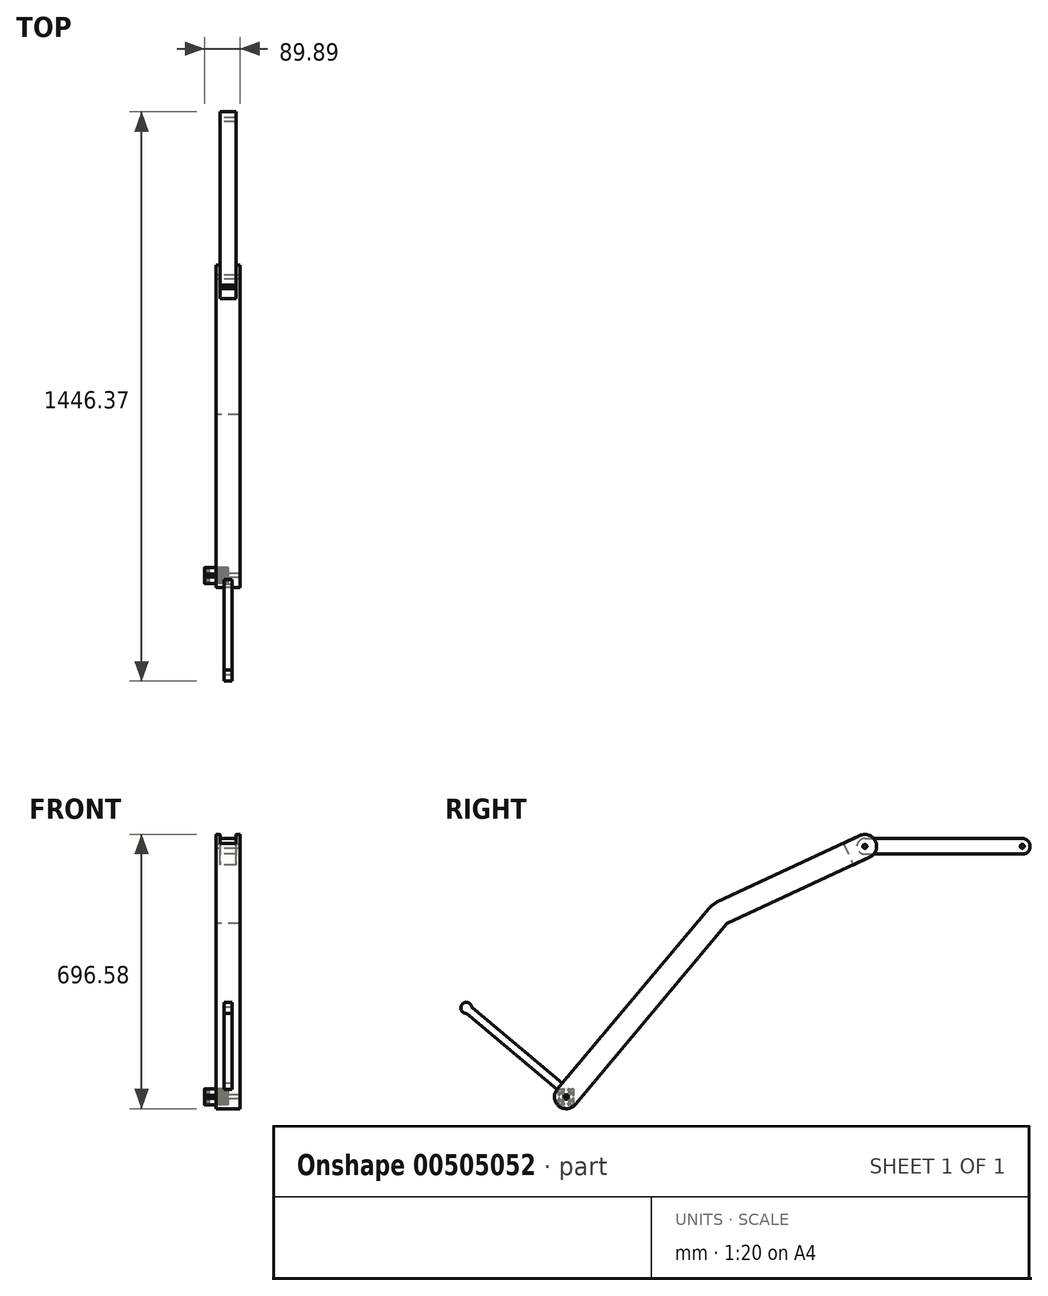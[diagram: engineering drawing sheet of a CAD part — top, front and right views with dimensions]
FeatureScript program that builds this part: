
annotation { "Feature Type Name" : "Feature", "Feature Type Description" : "" }
export const myFeature = defineFeature(function(context is Context, id is Id, definition is map)
    precondition{}
    {
        {
            var Q0;
            Q0=qCreatedBy(makeId("Right.planeOp"),FACE);
            var sketch = newSketch(context, id + "F0", { "sketchPlane" : qUnion([Q0])});
            skCircle(sketch, "E0", {"center": v(0, 0) * mm, "radius": 5 * mm});
            skArc(sketch, "E1", {"start": v(-22.98, 19.28) * mm, "mid": v(-19.28, -22.98) * mm, "end": v(22.98, -19.28) * mm});
            skLineSegment(sketch, "E2", {"start": v(-22.98, 19.28) * mm, "end": v(362.7, 478.91) * mm});
            skLineSegment(sketch, "E3", {"start": v(22.98, -19.28) * mm, "end": v(408.65, 440.34) * mm});
            skLineSegment(sketch, "E4", {"start": v(0, 0) * mm, "end": v(-104.18, 0) * mm, "construction": true});
            skLineSegment(sketch, "E5", {"start": v(408.65, 440.34) * mm, "end": v(771.18, 609.4) * mm});
            skLineSegment(sketch, "E6", {"start": v(745.82, 663.77) * mm, "end": v(383.3, 494.72) * mm});
            skArc(sketch, "E7", {"start": v(362.7, 478.91) * mm, "mid": v(372.13, 487.94) * mm, "end": v(383.3, 494.72) * mm});
            skLineSegment(sketch, "E8", {"start": v(383.3, 494.72) * mm, "end": v(408.65, 440.34) * mm, "construction": true});
            skArc(sketch, "E9", {"start": v(745.82, 663.77) * mm, "mid": v(785.69, 649.26) * mm, "end": v(771.18, 609.4) * mm});
            skCircle(sketch, "E10", {"center": v(758.5, 636.58) * mm, "radius": 5 * mm});
            skLineSegment(sketch, "E11", {"start": v(-22.98, 19.28) * mm, "end": v(-252.8, 212.12) * mm});
            skLineSegment(sketch, "E12", {"start": v(-252.8, 212.12) * mm, "end": v(-239.94, 227.44) * mm, "construction": true});
            skLineSegment(sketch, "E13", {"start": v(-239.94, 227.44) * mm, "end": v(-10.13, 34.6) * mm});
            skArc(sketch, "E14", {"start": v(-239.94, 227.44) * mm, "mid": v(-264.6, 235.08) * mm, "end": v(-252.8, 212.12) * mm});
            skSolve(sketch);
        }
        {
            var Q0;
            Q0=qCreatedBy(makeId("Right.planeOp"),FACE);
            var sketch = newSketch(context, id + "F1", { "sketchPlane" : qUnion([Q0])});
            skPoint(sketch, "E15.0", {"position": v(758.5, 636.58) * mm});
            skCircle(sketch, "E16.0", {"center": v(758.5, 636.58) * mm, "radius": 5 * mm});
            skLineSegment(sketch, "E17", {"start": v(758.5, 636.58) * mm, "end": v(758.5, 656.58) * mm});
            skArc(sketch, "E18", {"start": v(758.5, 656.58) * mm, "mid": v(738.5, 636.58) * mm, "end": v(758.5, 616.58) * mm});
            skLineSegment(sketch, "E19", {"start": v(758.5, 656.58) * mm, "end": v(1158.5, 656.58) * mm});
            skLineSegment(sketch, "E20", {"start": v(758.5, 616.58) * mm, "end": v(1158.5, 616.58) * mm});
            skLineSegment(sketch, "E21", {"start": v(1158.5, 656.58) * mm, "end": v(1158.5, 616.58) * mm, "construction": true});
            skArc(sketch, "E22", {"start": v(1158.5, 656.58) * mm, "mid": v(1178.5, 636.58) * mm, "end": v(1158.5, 616.58) * mm});
            skCircle(sketch, "E23", {"center": v(1158.5, 636.58) * mm, "radius": 5 * mm});
            skSolve(sketch);
        }
        {
            var Q0;
            Q0=makeQuery(id+"F0.imprint","IMPRINT",FACE,{"disambiguationData":[TD([[makeQuery(id+"F0.imprint","IMPRINT",EDGE,{"derivedFrom":sQuery(id+"F0.wireOp",EDGE,"E0")}),-1.0]])]});
            extrude(context, id + "F2", {"entities" : qUnion([Q0]), "endBound" : BoundingType.SYMMETRIC, "depth" : 60 * mm});
        }
        {
            var Q0;
            Q0=makeQuery(id+"F2.opExtrude","CAP_VERTEX",VERTEX,{"disambiguationData":[OSD([sQuery(id+"F0.wireOp",EDGE,"E6"),sQuery(id+"F0.wireOp",EDGE,"E9")])],"isStart":false});
            var Q1;
            Q1=makeQuery(id+"F2.opExtrude","CAP_VERTEX",VERTEX,{"disambiguationData":[OSD([sQuery(id+"F0.wireOp",EDGE,"E5"),sQuery(id+"F0.wireOp",EDGE,"E9")])],"isStart":false});
            var Q2;
            Q2=makeQuery(id+"F2.opExtrude","CAP_VERTEX",VERTEX,{"disambiguationData":[OSD([sQuery(id+"F0.wireOp",EDGE,"E5"),sQuery(id+"F0.wireOp",EDGE,"E9")])],"isStart":true});
            cPlane(context, id + "F3", {"entities" : qUnion([Q0, Q1, Q2]), "cplaneType" : CPlaneType.THREE_POINT, "offset" : 25 * mm, "width" : 150 * mm, "height" : 150 * mm});
        }
        {
            var Q0;
            Q0=qCreatedBy(id+"F3.planeOp",FACE);
            var sketch = newSketch(context, id + "F4", { "sketchPlane" : qUnion([Q0])});
            skPoint(sketch, "E24.0", {"position": v(0, 256.38) * mm});
            skLineSegment(sketch, "E25", {"start": v(0, 256.38) * mm, "end": v(20, 256.38) * mm, "construction": true});
            skLineSegment(sketch, "E26.0", {"start": v(30, 286.38) * mm, "end": v(-30, 286.38) * mm, "construction": true});
            skLineSegment(sketch, "E27.0", {"start": v(30, 226.38) * mm, "end": v(-30, 226.38) * mm, "construction": true});
            skLineSegment(sketch, "E28.bottom", {"start": v(20, 286.38) * mm, "end": v(-20, 286.38) * mm});
            skLineSegment(sketch, "E28.top", {"start": v(20, 226.38) * mm, "end": v(-20, 226.38) * mm});
            skLineSegment(sketch, "E28.left", {"start": v(20, 286.38) * mm, "end": v(20, 226.38) * mm});
            skLineSegment(sketch, "E28.right", {"start": v(-20, 286.38) * mm, "end": v(-20, 226.38) * mm});
            skSolve(sketch);
        }
        {
            var Q0;
            Q0 = qSketchRegion(id + "F4", true);
            extrude(context, id + "F5", {"entities" : qUnion([Q0]), "operationType" : NewBodyOperationType.REMOVE, "depth" : 46.5 * mm, "hasSecondDirection" : true, "secondDirectionOppositeDirection" : true, "secondDirectionDepth" : 41.1 * mm});
        }
        {
            var Q0;
            Q0 = qSketchRegion(id + "F1", true);
            extrude(context, id + "F6", {"entities" : qUnion([Q0]), "endBound" : BoundingType.SYMMETRIC, "depth" : 40 * mm});
        }
        {
            var Q0;
            Q0=qCreatedBy(makeId("Right.planeOp"),FACE);
            var sketch = newSketch(context, id + "F7", { "sketchPlane" : qUnion([Q0])});
            skCircle(sketch, "E29.0", {"center": v(0, 0) * mm, "radius": 5 * mm});
            skSolve(sketch);
        }
        {
            var Q0;
            Q0 = qSketchRegion(id + "F7", true);
            extrude(context, id + "F8", {"entities" : qUnion([Q0]), "endBound" : BoundingType.SYMMETRIC, "depth" : 60 * mm});
        }
        {
            var Q0;
            Q0=makeQuery(id+"F8.opExtrude","CAP_EDGE",EDGE,{"disambiguationData":[OSD([sQuery(id+"F7.wireOp",EDGE,"E29.0")])],"isStart":true});
            var Q1;
            Q1=makeQuery(id+"F8.opExtrude","CAP_EDGE",EDGE,{"disambiguationData":[OSD([sQuery(id+"F7.wireOp",EDGE,"E29.0")])],"isStart":false});
            chamfer(context, id + "F9", {"entities" : qUnion([Q0, Q1]), "width" : 1 * mm, "tangentPropagation" : true});
        }
        {
            var Q0;
            {var subQ0=sQuery(id+"F0.wireOp",EDGE,"E11");Q0=makeQuery(id+"F0.imprint","IMPRINT",FACE,{"disambiguationData":[TD([[makeQuery(id+"F0.imprint","IMPRINT",EDGE,{"derivedFrom":subQ0}),-1.0]])]});}
            extrude(context, id + "F10", {"entities" : qUnion([Q0]), "operationType" : NewBodyOperationType.ADD, "endBound" : BoundingType.SYMMETRIC, "depth" : 20 * mm});
        }
        {
            var Q0;
            Q0=qCreatedBy(makeId("Right.planeOp"),FACE);
            var sketch = newSketch(context, id + "F11", { "sketchPlane" : qUnion([Q0])});
            skLineSegment(sketch, "E30", {"start": v(-10.29, 12.4) * mm, "end": v(-10.55, 12.74) * mm});
            skLineSegment(sketch, "E31", {"start": v(10.55, -12.74) * mm, "end": v(10.29, -12.4) * mm});
            skLineSegment(sketch, "E32", {"start": v(10.76, 9.6) * mm, "end": v(9.6, 10.76) * mm});
            skLineSegment(sketch, "E33", {"start": v(-10.33, -11.73) * mm, "end": v(-11.73, -10.33) * mm});
            skLineSegment(sketch, "E34", {"start": v(-9.6, -10.76) * mm, "end": v(-10.76, -9.6) * mm});
            skLineSegment(sketch, "E35", {"start": v(11.73, 10.33) * mm, "end": v(10.33, 11.73) * mm});
            skLineSegment(sketch, "E36", {"start": v(12.74, -10.55) * mm, "end": v(12.4, -10.29) * mm});
            skLineSegment(sketch, "E37", {"start": v(-12.4, 10.29) * mm, "end": v(-12.74, 10.55) * mm});
            skLineSegment(sketch, "E38", {"start": v(-16, -20) * mm, "end": v(-5.5, -20) * mm});
            skLineSegment(sketch, "E39", {"start": v(5.5, -20) * mm, "end": v(16, -20) * mm});
            skLineSegment(sketch, "E40", {"start": v(-16, -18.8) * mm, "end": v(-11.7, -18.8) * mm});
            skLineSegment(sketch, "E41", {"start": v(11.7, -18.8) * mm, "end": v(16, -18.8) * mm});
            skLineSegment(sketch, "E42", {"start": v(-7.5, -18) * mm, "end": v(-7.25, -18) * mm});
            skLineSegment(sketch, "E43", {"start": v(7.25, -18) * mm, "end": v(7.5, -18) * mm});
            skLineSegment(sketch, "E44", {"start": v(-6.75, -15.5) * mm, "end": v(-5, -15.5) * mm});
            skLineSegment(sketch, "E45", {"start": v(5, -15.5) * mm, "end": v(6.75, -15.5) * mm});
            skLineSegment(sketch, "E46", {"start": v(-18.3, -11.2) * mm, "end": v(-14.67, -11.2) * mm});
            skLineSegment(sketch, "E47", {"start": v(14.67, -11.2) * mm, "end": v(18.3, -11.2) * mm});
            skLineSegment(sketch, "E48", {"start": v(-15.5, -10) * mm, "end": v(-14.72, -10) * mm});
            skLineSegment(sketch, "E49", {"start": v(14.72, -10) * mm, "end": v(15.5, -10) * mm});
            skLineSegment(sketch, "E50", {"start": v(-2.2, -7.75) * mm, "end": v(2.2, -7.75) * mm});
            skLineSegment(sketch, "E51", {"start": v(-17.75, -7) * mm, "end": v(-15.75, -7) * mm});
            skLineSegment(sketch, "E52", {"start": v(15.75, -7) * mm, "end": v(17.75, -7) * mm});
            skLineSegment(sketch, "E53", {"start": v(-18.5, -4) * mm, "end": v(-16.5, -4) * mm});
            skLineSegment(sketch, "E54", {"start": v(16.5, -4) * mm, "end": v(18.5, -4) * mm});
            skLineSegment(sketch, "E55", {"start": v(-6.1, -2.5) * mm, "end": v(-4.6, -2.5) * mm});
            skLineSegment(sketch, "E56", {"start": v(4.6, -2.5) * mm, "end": v(6.1, -2.5) * mm});
            skLineSegment(sketch, "E57", {"start": v(4.6, 2.5) * mm, "end": v(6.1, 2.5) * mm});
            skLineSegment(sketch, "E58", {"start": v(-6.1, 2.5) * mm, "end": v(-4.6, 2.5) * mm});
            skLineSegment(sketch, "E59", {"start": v(-18.5, 4) * mm, "end": v(-16.5, 4) * mm});
            skLineSegment(sketch, "E60", {"start": v(16.5, 4) * mm, "end": v(18.5, 4) * mm});
            skLineSegment(sketch, "E61", {"start": v(-17.75, 7) * mm, "end": v(-15.75, 7) * mm});
            skLineSegment(sketch, "E62", {"start": v(15.75, 7) * mm, "end": v(17.75, 7) * mm});
            skLineSegment(sketch, "E63", {"start": v(-2.2, 7.75) * mm, "end": v(2.2, 7.75) * mm});
            skLineSegment(sketch, "E64", {"start": v(-15.5, 10) * mm, "end": v(-14.72, 10) * mm});
            skLineSegment(sketch, "E65", {"start": v(14.72, 10) * mm, "end": v(15.5, 10) * mm});
            skLineSegment(sketch, "E66", {"start": v(-18.3, 11.2) * mm, "end": v(-14.67, 11.2) * mm});
            skLineSegment(sketch, "E67", {"start": v(14.67, 11.2) * mm, "end": v(18.3, 11.2) * mm});
            skLineSegment(sketch, "E68", {"start": v(-6.75, 15.5) * mm, "end": v(-5, 15.5) * mm});
            skLineSegment(sketch, "E69", {"start": v(5, 15.5) * mm, "end": v(6.75, 15.5) * mm});
            skLineSegment(sketch, "E70", {"start": v(-7.5, 18) * mm, "end": v(-7.25, 18) * mm});
            skLineSegment(sketch, "E71", {"start": v(7.25, 18) * mm, "end": v(7.5, 18) * mm});
            skLineSegment(sketch, "E72", {"start": v(-16, 18.8) * mm, "end": v(-11.7, 18.8) * mm});
            skLineSegment(sketch, "E73", {"start": v(11.7, 18.8) * mm, "end": v(16, 18.8) * mm});
            skLineSegment(sketch, "E74", {"start": v(5.5, 20) * mm, "end": v(16, 20) * mm});
            skLineSegment(sketch, "E75", {"start": v(-16, 20) * mm, "end": v(-5.5, 20) * mm});
            skLineSegment(sketch, "E76", {"start": v(12.4, 10.29) * mm, "end": v(12.74, 10.55) * mm});
            skLineSegment(sketch, "E77", {"start": v(-12.74, -10.55) * mm, "end": v(-12.4, -10.29) * mm});
            skLineSegment(sketch, "E78", {"start": v(9.6, -10.76) * mm, "end": v(10.76, -9.6) * mm});
            skLineSegment(sketch, "E79", {"start": v(-10.76, 9.6) * mm, "end": v(-9.6, 10.76) * mm});
            skLineSegment(sketch, "E80", {"start": v(10.33, -11.73) * mm, "end": v(11.73, -10.33) * mm});
            skLineSegment(sketch, "E81", {"start": v(-11.73, 10.33) * mm, "end": v(-10.33, 11.73) * mm});
            skLineSegment(sketch, "E82", {"start": v(10.29, 12.4) * mm, "end": v(10.55, 12.74) * mm});
            skLineSegment(sketch, "E83", {"start": v(-10.55, -12.74) * mm, "end": v(-10.29, -12.4) * mm});
            skLineSegment(sketch, "E84", {"start": v(-20, 5.5) * mm, "end": v(-20, 16) * mm});
            skLineSegment(sketch, "E85", {"start": v(-20, -16) * mm, "end": v(-20, -5.5) * mm});
            skLineSegment(sketch, "E86", {"start": v(-18.8, 11.7) * mm, "end": v(-18.8, 16) * mm});
            skLineSegment(sketch, "E87", {"start": v(-18.8, -16) * mm, "end": v(-18.8, -11.7) * mm});
            skLineSegment(sketch, "E88", {"start": v(-18, 7.25) * mm, "end": v(-18, 7.5) * mm});
            skLineSegment(sketch, "E89", {"start": v(-18, -7.5) * mm, "end": v(-18, -7.25) * mm});
            skLineSegment(sketch, "E90", {"start": v(-15.5, 5) * mm, "end": v(-15.5, 6.75) * mm});
            skLineSegment(sketch, "E91", {"start": v(-15.5, -6.75) * mm, "end": v(-15.5, -5) * mm});
            skLineSegment(sketch, "E92", {"start": v(-11.2, 14.67) * mm, "end": v(-11.2, 18.3) * mm});
            skLineSegment(sketch, "E93", {"start": v(-11.2, -18.3) * mm, "end": v(-11.2, -14.67) * mm});
            skLineSegment(sketch, "E94", {"start": v(-10, 14.72) * mm, "end": v(-10, 15.5) * mm});
            skLineSegment(sketch, "E95", {"start": v(-10, -15.5) * mm, "end": v(-10, -14.72) * mm});
            skLineSegment(sketch, "E96", {"start": v(-7.75, -2.2) * mm, "end": v(-7.75, 2.2) * mm});
            skLineSegment(sketch, "E97", {"start": v(-7, 15.75) * mm, "end": v(-7, 17.75) * mm});
            skLineSegment(sketch, "E98", {"start": v(-7, -17.75) * mm, "end": v(-7, -15.75) * mm});
            skLineSegment(sketch, "E99", {"start": v(-4, 16.5) * mm, "end": v(-4, 18.5) * mm});
            skLineSegment(sketch, "E100", {"start": v(-4, -18.5) * mm, "end": v(-4, -16.5) * mm});
            skLineSegment(sketch, "E101", {"start": v(-2.5, 4.6) * mm, "end": v(-2.5, 6.1) * mm});
            skLineSegment(sketch, "E102", {"start": v(-2.5, -6.1) * mm, "end": v(-2.5, -4.6) * mm});
            skLineSegment(sketch, "E103", {"start": v(2.5, 4.6) * mm, "end": v(2.5, 6.1) * mm});
            skLineSegment(sketch, "E104", {"start": v(2.5, -6.1) * mm, "end": v(2.5, -4.6) * mm});
            skLineSegment(sketch, "E105", {"start": v(4, 16.5) * mm, "end": v(4, 18.5) * mm});
            skLineSegment(sketch, "E106", {"start": v(4, -18.5) * mm, "end": v(4, -16.5) * mm});
            skLineSegment(sketch, "E107", {"start": v(7, 15.75) * mm, "end": v(7, 17.75) * mm});
            skLineSegment(sketch, "E108", {"start": v(7, -17.75) * mm, "end": v(7, -15.75) * mm});
            skLineSegment(sketch, "E109", {"start": v(7.75, -2.2) * mm, "end": v(7.75, 2.2) * mm});
            skLineSegment(sketch, "E110", {"start": v(10, 14.72) * mm, "end": v(10, 15.5) * mm});
            skLineSegment(sketch, "E111", {"start": v(10, -15.5) * mm, "end": v(10, -14.72) * mm});
            skLineSegment(sketch, "E112", {"start": v(11.2, 14.67) * mm, "end": v(11.2, 18.3) * mm});
            skLineSegment(sketch, "E113", {"start": v(11.2, -18.3) * mm, "end": v(11.2, -14.67) * mm});
            skLineSegment(sketch, "E114", {"start": v(15.5, -6.75) * mm, "end": v(15.5, -5) * mm});
            skLineSegment(sketch, "E115", {"start": v(15.5, 5) * mm, "end": v(15.5, 6.75) * mm});
            skLineSegment(sketch, "E116", {"start": v(18, -7.5) * mm, "end": v(18, -7.25) * mm});
            skLineSegment(sketch, "E117", {"start": v(18, 7.25) * mm, "end": v(18, 7.5) * mm});
            skLineSegment(sketch, "E118", {"start": v(18.8, 11.7) * mm, "end": v(18.8, 16) * mm});
            skLineSegment(sketch, "E119", {"start": v(18.8, -16) * mm, "end": v(18.8, -11.7) * mm});
            skLineSegment(sketch, "E120", {"start": v(20, -16) * mm, "end": v(20, -5.5) * mm});
            skLineSegment(sketch, "E121", {"start": v(20, 5.5) * mm, "end": v(20, 16) * mm});
            skArc(sketch, "E122", {"start": v(-8.54, 4.58) * mm, "mid": v(-10.85, 7.26) * mm, "end": v(-13.51, 9.6) * mm});
            skArc(sketch, "E123", {"start": v(-13.51, -9.6) * mm, "mid": v(-10.85, -7.26) * mm, "end": v(-8.54, -4.58) * mm});
            skArc(sketch, "E124", {"start": v(-7.6, 5.38) * mm, "mid": v(-9.09, 7.2) * mm, "end": v(-10.75, 8.88) * mm});
            skArc(sketch, "E125", {"start": v(-10.75, -8.88) * mm, "mid": v(-9.09, -7.2) * mm, "end": v(-7.6, -5.38) * mm});
            skArc(sketch, "E126", {"start": v(-18.5, -4) * mm, "mid": v(-19.56, -4.44) * mm, "end": v(-20, -5.5) * mm});
            skArc(sketch, "E127", {"start": v(-20, 5.5) * mm, "mid": v(-19.56, 4.44) * mm, "end": v(-18.5, 4) * mm});
            skArc(sketch, "E128", {"start": v(-18.8, 11.7) * mm, "mid": v(-18.65, 11.35) * mm, "end": v(-18.3, 11.2) * mm});
            skArc(sketch, "E129", {"start": v(-18.3, -11.2) * mm, "mid": v(-18.65, -11.35) * mm, "end": v(-18.8, -11.7) * mm});
            skArc(sketch, "E130", {"start": v(-17.75, -7) * mm, "mid": v(-17.93, -7.07) * mm, "end": v(-18, -7.25) * mm});
            skArc(sketch, "E131", {"start": v(-18, 7.25) * mm, "mid": v(-17.93, 7.07) * mm, "end": v(-17.75, 7) * mm});
            skArc(sketch, "E132", {"start": v(-15.5, -5) * mm, "mid": v(-15.8, -4.3) * mm, "end": v(-16.5, -4) * mm});
            skArc(sketch, "E133", {"start": v(-16.5, 4) * mm, "mid": v(-15.8, 4.3) * mm, "end": v(-15.5, 5) * mm});
            skArc(sketch, "E134", {"start": v(-20, -16) * mm, "mid": v(-18.83, -18.83) * mm, "end": v(-16, -20) * mm});
            skArc(sketch, "E135", {"start": v(-16, 18.8) * mm, "mid": v(-17.98, 17.98) * mm, "end": v(-18.8, 16) * mm});
            skArc(sketch, "E136", {"start": v(-16, 20) * mm, "mid": v(-18.83, 18.83) * mm, "end": v(-20, 16) * mm});
            skArc(sketch, "E137", {"start": v(-18.8, -16) * mm, "mid": v(-17.98, -17.98) * mm, "end": v(-16, -18.8) * mm});
            skArc(sketch, "E138", {"start": v(-15.75, -7) * mm, "mid": v(-15.57, -6.93) * mm, "end": v(-15.5, -6.75) * mm});
            skArc(sketch, "E139", {"start": v(-15.5, 6.75) * mm, "mid": v(-15.57, 6.93) * mm, "end": v(-15.75, 7) * mm});
            skArc(sketch, "E140", {"start": v(-18, -7.5) * mm, "mid": v(-17.27, -9.27) * mm, "end": v(-15.5, -10) * mm});
            skArc(sketch, "E141", {"start": v(-15.5, 10) * mm, "mid": v(-17.27, 9.27) * mm, "end": v(-18, 7.5) * mm});
            skArc(sketch, "E142", {"start": v(-14.72, -10) * mm, "mid": v(-14.08, -9.9) * mm, "end": v(-13.51, -9.6) * mm});
            skArc(sketch, "E143", {"start": v(-13.51, 9.6) * mm, "mid": v(-14.08, 9.9) * mm, "end": v(-14.72, 10) * mm});
            skArc(sketch, "E144", {"start": v(-12.74, 10.55) * mm, "mid": v(-13.65, 11.03) * mm, "end": v(-14.67, 11.2) * mm});
            skArc(sketch, "E145", {"start": v(-14.67, -11.2) * mm, "mid": v(-13.65, -11.03) * mm, "end": v(-12.74, -10.55) * mm});
            skArc(sketch, "E146", {"start": v(-12.4, 10.29) * mm, "mid": v(-12.06, 10.18) * mm, "end": v(-11.73, 10.33) * mm});
            skArc(sketch, "E147", {"start": v(-11.73, -10.33) * mm, "mid": v(-12.06, -10.18) * mm, "end": v(-12.4, -10.29) * mm});
            skArc(sketch, "E148", {"start": v(-7.59, -5.38) * mm, "mid": v(-6.93, -4.22) * mm, "end": v(-6.6, -2.94) * mm});
            skArc(sketch, "E149", {"start": v(-8.54, -4.58) * mm, "mid": v(-7.95, -3.45) * mm, "end": v(-7.75, -2.2) * mm});
            skArc(sketch, "E150", {"start": v(-7.75, 2.2) * mm, "mid": v(-7.95, 3.45) * mm, "end": v(-8.54, 4.58) * mm});
            skArc(sketch, "E151", {"start": v(-6.6, 2.94) * mm, "mid": v(-6.93, 4.22) * mm, "end": v(-7.6, 5.38) * mm});
            skArc(sketch, "E152", {"start": v(-11.2, 18.3) * mm, "mid": v(-11.35, 18.65) * mm, "end": v(-11.7, 18.8) * mm});
            skArc(sketch, "E153", {"start": v(-11.7, -18.8) * mm, "mid": v(-11.35, -18.65) * mm, "end": v(-11.2, -18.3) * mm});
            skArc(sketch, "E154", {"start": v(-10.33, 11.73) * mm, "mid": v(-10.18, 12.06) * mm, "end": v(-10.29, 12.4) * mm});
            skArc(sketch, "E155", {"start": v(-10.29, -12.4) * mm, "mid": v(-10.18, -12.06) * mm, "end": v(-10.33, -11.73) * mm});
            skArc(sketch, "E156", {"start": v(-10.75, -8.88) * mm, "mid": v(-10.9, -9.24) * mm, "end": v(-10.76, -9.6) * mm});
            skArc(sketch, "E157", {"start": v(-10.76, 9.6) * mm, "mid": v(-10.9, 9.24) * mm, "end": v(-10.75, 8.88) * mm});
            skArc(sketch, "E158", {"start": v(9.6, -13.51) * mm, "mid": v(7.26, -10.85) * mm, "end": v(4.58, -8.54) * mm});
            skArc(sketch, "E159", {"start": v(8.88, -10.75) * mm, "mid": v(7.2, -9.09) * mm, "end": v(5.38, -7.6) * mm});
            skArc(sketch, "E160", {"start": v(5.38, 7.59) * mm, "mid": v(7.2, 9.09) * mm, "end": v(8.88, 10.75) * mm});
            skArc(sketch, "E161", {"start": v(4.58, 8.54) * mm, "mid": v(7.26, 10.85) * mm, "end": v(9.6, 13.51) * mm});
            skArc(sketch, "E162", {"start": v(-9.6, -10.76) * mm, "mid": v(-9.24, -10.9) * mm, "end": v(-8.88, -10.75) * mm});
            skArc(sketch, "E163", {"start": v(-8.88, 10.75) * mm, "mid": v(-9.24, 10.9) * mm, "end": v(-9.6, 10.76) * mm});
            skArc(sketch, "E164", {"start": v(-9.6, -13.51) * mm, "mid": v(-9.9, -14.08) * mm, "end": v(-10, -14.72) * mm});
            skArc(sketch, "E165", {"start": v(-11.2, 14.67) * mm, "mid": v(-11.03, 13.65) * mm, "end": v(-10.55, 12.74) * mm});
            skArc(sketch, "E166", {"start": v(-10, 14.72) * mm, "mid": v(-9.9, 14.08) * mm, "end": v(-9.6, 13.51) * mm});
            skArc(sketch, "E167", {"start": v(-10.55, -12.74) * mm, "mid": v(-11.03, -13.65) * mm, "end": v(-11.2, -14.67) * mm});
            skArc(sketch, "E168", {"start": v(-10, -15.5) * mm, "mid": v(-9.27, -17.27) * mm, "end": v(-7.5, -18) * mm});
            skArc(sketch, "E169", {"start": v(-7.5, 18) * mm, "mid": v(-9.27, 17.27) * mm, "end": v(-10, 15.5) * mm});
            skArc(sketch, "E170", {"start": v(-7.25, -18) * mm, "mid": v(-7.07, -17.93) * mm, "end": v(-7, -17.75) * mm});
            skArc(sketch, "E171", {"start": v(-7, 17.75) * mm, "mid": v(-7.07, 17.93) * mm, "end": v(-7.25, 18) * mm});
            skArc(sketch, "E172", {"start": v(-6.75, -15.5) * mm, "mid": v(-6.93, -15.57) * mm, "end": v(-7, -15.75) * mm});
            skArc(sketch, "E173", {"start": v(-7, 15.75) * mm, "mid": v(-6.93, 15.57) * mm, "end": v(-6.75, 15.5) * mm});
            skArc(sketch, "E174", {"start": v(-6.1, -2.5) * mm, "mid": v(-6.43, -2.62) * mm, "end": v(-6.6, -2.94) * mm});
            skArc(sketch, "E175", {"start": v(-6.6, 2.94) * mm, "mid": v(-6.43, 2.62) * mm, "end": v(-6.1, 2.5) * mm});
            skArc(sketch, "E176", {"start": v(-5.5, -20) * mm, "mid": v(-4.44, -19.56) * mm, "end": v(-4, -18.5) * mm});
            skArc(sketch, "E177", {"start": v(-4, 18.5) * mm, "mid": v(-4.44, 19.56) * mm, "end": v(-5.5, 20) * mm});
            skArc(sketch, "E178", {"start": v(-4, -16.5) * mm, "mid": v(-4.3, -15.8) * mm, "end": v(-5, -15.5) * mm});
            skArc(sketch, "E179", {"start": v(-5, 15.5) * mm, "mid": v(-4.3, 15.8) * mm, "end": v(-4, 16.5) * mm});
            skArc(sketch, "E180", {"start": v(-4.2, -2.73) * mm, "mid": v(-4.37, -2.56) * mm, "end": v(-4.6, -2.5) * mm});
            skArc(sketch, "E181", {"start": v(-4.6, 2.5) * mm, "mid": v(-4.37, 2.56) * mm, "end": v(-4.2, 2.73) * mm});
            skArc(sketch, "E182", {"start": v(-2.94, -6.6) * mm, "mid": v(-2.62, -6.43) * mm, "end": v(-2.5, -6.1) * mm});
            skArc(sketch, "E183", {"start": v(-2.5, -4.6) * mm, "mid": v(-2.56, -4.37) * mm, "end": v(-2.73, -4.2) * mm});
            skArc(sketch, "E184", {"start": v(-2.73, 4.2) * mm, "mid": v(-2.56, 4.37) * mm, "end": v(-2.5, 4.6) * mm});
            skArc(sketch, "E185", {"start": v(-2.5, 6.1) * mm, "mid": v(-2.62, 6.43) * mm, "end": v(-2.94, 6.6) * mm});
            skArc(sketch, "E186", {"start": v(-2.94, -6.6) * mm, "mid": v(-4.22, -6.93) * mm, "end": v(-5.38, -7.6) * mm});
            skArc(sketch, "E187", {"start": v(-5.38, 7.59) * mm, "mid": v(-4.22, 6.93) * mm, "end": v(-2.94, 6.6) * mm});
            skArc(sketch, "E188", {"start": v(-2.2, -7.75) * mm, "mid": v(-3.45, -7.95) * mm, "end": v(-4.58, -8.54) * mm});
            skArc(sketch, "E189", {"start": v(-4.58, 8.54) * mm, "mid": v(-3.45, 7.95) * mm, "end": v(-2.2, 7.75) * mm});
            skCircle(sketch, "E190", {"center": v(0, 0) * mm, "radius": 3.4 * mm});
            skArc(sketch, "E191", {"start": v(4.2, 2.73) * mm, "mid": v(3.54, 3.54) * mm, "end": v(2.73, 4.2) * mm});
            skArc(sketch, "E192", {"start": v(-2.73, 4.2) * mm, "mid": v(-3.54, 3.54) * mm, "end": v(-4.2, 2.73) * mm});
            skArc(sketch, "E193", {"start": v(-4.2, -2.73) * mm, "mid": v(-3.54, -3.54) * mm, "end": v(-2.73, -4.2) * mm});
            skArc(sketch, "E194", {"start": v(2.73, -4.2) * mm, "mid": v(3.54, -3.54) * mm, "end": v(4.2, -2.73) * mm});
            skArc(sketch, "E195", {"start": v(4.58, -8.54) * mm, "mid": v(3.45, -7.95) * mm, "end": v(2.2, -7.75) * mm});
            skArc(sketch, "E196", {"start": v(2.2, 7.75) * mm, "mid": v(3.45, 7.95) * mm, "end": v(4.58, 8.54) * mm});
            skArc(sketch, "E197", {"start": v(5.38, -7.59) * mm, "mid": v(4.22, -6.93) * mm, "end": v(2.94, -6.6) * mm});
            skArc(sketch, "E198", {"start": v(2.94, 6.6) * mm, "mid": v(4.22, 6.93) * mm, "end": v(5.38, 7.6) * mm});
            skArc(sketch, "E199", {"start": v(2.5, -6.1) * mm, "mid": v(2.62, -6.43) * mm, "end": v(2.94, -6.6) * mm});
            skArc(sketch, "E200", {"start": v(2.73, -4.2) * mm, "mid": v(2.56, -4.37) * mm, "end": v(2.5, -4.6) * mm});
            skArc(sketch, "E201", {"start": v(2.5, 4.6) * mm, "mid": v(2.56, 4.37) * mm, "end": v(2.73, 4.2) * mm});
            skArc(sketch, "E202", {"start": v(2.94, 6.6) * mm, "mid": v(2.62, 6.43) * mm, "end": v(2.5, 6.1) * mm});
            skArc(sketch, "E203", {"start": v(4.6, -2.5) * mm, "mid": v(4.37, -2.56) * mm, "end": v(4.2, -2.73) * mm});
            skArc(sketch, "E204", {"start": v(4.2, 2.73) * mm, "mid": v(4.37, 2.56) * mm, "end": v(4.6, 2.5) * mm});
            skArc(sketch, "E205", {"start": v(5, -15.5) * mm, "mid": v(4.3, -15.8) * mm, "end": v(4, -16.5) * mm});
            skArc(sketch, "E206", {"start": v(4, 16.5) * mm, "mid": v(4.3, 15.8) * mm, "end": v(5, 15.5) * mm});
            skArc(sketch, "E207", {"start": v(4, -18.5) * mm, "mid": v(4.44, -19.56) * mm, "end": v(5.5, -20) * mm});
            skArc(sketch, "E208", {"start": v(5.5, 20) * mm, "mid": v(4.44, 19.56) * mm, "end": v(4, 18.5) * mm});
            skArc(sketch, "E209", {"start": v(6.6, -2.94) * mm, "mid": v(6.43, -2.62) * mm, "end": v(6.1, -2.5) * mm});
            skArc(sketch, "E210", {"start": v(6.1, 2.5) * mm, "mid": v(6.43, 2.62) * mm, "end": v(6.6, 2.94) * mm});
            skArc(sketch, "E211", {"start": v(7, -15.75) * mm, "mid": v(6.93, -15.57) * mm, "end": v(6.75, -15.5) * mm});
            skArc(sketch, "E212", {"start": v(6.75, 15.5) * mm, "mid": v(6.93, 15.57) * mm, "end": v(7, 15.75) * mm});
            skArc(sketch, "E213", {"start": v(7, -17.75) * mm, "mid": v(7.07, -17.93) * mm, "end": v(7.25, -18) * mm});
            skArc(sketch, "E214", {"start": v(7.25, 18) * mm, "mid": v(7.07, 17.93) * mm, "end": v(7, 17.75) * mm});
            skArc(sketch, "E215", {"start": v(7.5, -18) * mm, "mid": v(9.27, -17.27) * mm, "end": v(10, -15.5) * mm});
            skArc(sketch, "E216", {"start": v(10, 15.5) * mm, "mid": v(9.27, 17.27) * mm, "end": v(7.5, 18) * mm});
            skArc(sketch, "E217", {"start": v(10.55, 12.74) * mm, "mid": v(11.03, 13.65) * mm, "end": v(11.2, 14.67) * mm});
            skArc(sketch, "E218", {"start": v(10, -14.72) * mm, "mid": v(9.9, -14.08) * mm, "end": v(9.6, -13.51) * mm});
            skArc(sketch, "E219", {"start": v(11.2, -14.67) * mm, "mid": v(11.03, -13.65) * mm, "end": v(10.55, -12.74) * mm});
            skArc(sketch, "E220", {"start": v(9.6, 13.51) * mm, "mid": v(9.9, 14.08) * mm, "end": v(10, 14.72) * mm});
            skArc(sketch, "E221", {"start": v(8.88, -10.75) * mm, "mid": v(9.24, -10.9) * mm, "end": v(9.6, -10.76) * mm});
            skArc(sketch, "E222", {"start": v(9.6, 10.76) * mm, "mid": v(9.24, 10.9) * mm, "end": v(8.88, 10.75) * mm});
            skArc(sketch, "E223", {"start": v(-4.58, -8.54) * mm, "mid": v(-7.26, -10.85) * mm, "end": v(-9.6, -13.51) * mm});
            skArc(sketch, "E224", {"start": v(-5.38, -7.6) * mm, "mid": v(-7.2, -9.09) * mm, "end": v(-8.88, -10.75) * mm});
            skArc(sketch, "E225", {"start": v(-8.88, 10.75) * mm, "mid": v(-7.2, 9.09) * mm, "end": v(-5.38, 7.6) * mm});
            skArc(sketch, "E226", {"start": v(-9.6, 13.51) * mm, "mid": v(-7.26, 10.85) * mm, "end": v(-4.58, 8.54) * mm});
            skArc(sketch, "E227", {"start": v(10.76, -9.6) * mm, "mid": v(10.9, -9.24) * mm, "end": v(10.75, -8.88) * mm});
            skArc(sketch, "E228", {"start": v(10.75, 8.88) * mm, "mid": v(10.9, 9.24) * mm, "end": v(10.76, 9.6) * mm});
            skArc(sketch, "E229", {"start": v(10.29, 12.4) * mm, "mid": v(10.18, 12.06) * mm, "end": v(10.33, 11.73) * mm});
            skArc(sketch, "E230", {"start": v(10.33, -11.73) * mm, "mid": v(10.18, -12.06) * mm, "end": v(10.29, -12.4) * mm});
            skArc(sketch, "E231", {"start": v(11.7, 18.8) * mm, "mid": v(11.35, 18.65) * mm, "end": v(11.2, 18.3) * mm});
            skArc(sketch, "E232", {"start": v(11.2, -18.3) * mm, "mid": v(11.35, -18.65) * mm, "end": v(11.7, -18.8) * mm});
            skArc(sketch, "E233", {"start": v(6.6, -2.94) * mm, "mid": v(6.93, -4.22) * mm, "end": v(7.6, -5.38) * mm});
            skArc(sketch, "E234", {"start": v(7.75, -2.2) * mm, "mid": v(7.95, -3.45) * mm, "end": v(8.54, -4.58) * mm});
            skArc(sketch, "E235", {"start": v(8.54, 4.58) * mm, "mid": v(7.95, 3.45) * mm, "end": v(7.75, 2.2) * mm});
            skArc(sketch, "E236", {"start": v(7.59, 5.38) * mm, "mid": v(6.93, 4.22) * mm, "end": v(6.6, 2.94) * mm});
            skArc(sketch, "E237", {"start": v(11.73, 10.33) * mm, "mid": v(12.06, 10.18) * mm, "end": v(12.4, 10.29) * mm});
            skArc(sketch, "E238", {"start": v(12.4, -10.29) * mm, "mid": v(12.06, -10.18) * mm, "end": v(11.73, -10.33) * mm});
            skArc(sketch, "E239", {"start": v(14.67, 11.2) * mm, "mid": v(13.65, 11.03) * mm, "end": v(12.74, 10.55) * mm});
            skArc(sketch, "E240", {"start": v(12.74, -10.55) * mm, "mid": v(13.65, -11.03) * mm, "end": v(14.67, -11.2) * mm});
            skArc(sketch, "E241", {"start": v(13.51, -9.6) * mm, "mid": v(14.08, -9.9) * mm, "end": v(14.72, -10) * mm});
            skArc(sketch, "E242", {"start": v(14.72, 10) * mm, "mid": v(14.08, 9.9) * mm, "end": v(13.51, 9.6) * mm});
            skArc(sketch, "E243", {"start": v(15.5, -10) * mm, "mid": v(17.27, -9.27) * mm, "end": v(18, -7.5) * mm});
            skArc(sketch, "E244", {"start": v(18, 7.5) * mm, "mid": v(17.27, 9.27) * mm, "end": v(15.5, 10) * mm});
            skArc(sketch, "E245", {"start": v(15.5, -6.75) * mm, "mid": v(15.57, -6.93) * mm, "end": v(15.75, -7) * mm});
            skArc(sketch, "E246", {"start": v(15.75, 7) * mm, "mid": v(15.57, 6.93) * mm, "end": v(15.5, 6.75) * mm});
            skArc(sketch, "E247", {"start": v(18.8, 16) * mm, "mid": v(17.98, 17.98) * mm, "end": v(16, 18.8) * mm});
            skArc(sketch, "E248", {"start": v(16, -20) * mm, "mid": v(18.83, -18.83) * mm, "end": v(20, -16) * mm});
            skArc(sketch, "E249", {"start": v(16, -18.8) * mm, "mid": v(17.98, -17.98) * mm, "end": v(18.8, -16) * mm});
            skArc(sketch, "E250", {"start": v(20, 16) * mm, "mid": v(18.83, 18.83) * mm, "end": v(16, 20) * mm});
            skArc(sketch, "E251", {"start": v(16.5, -4) * mm, "mid": v(15.8, -4.3) * mm, "end": v(15.5, -5) * mm});
            skArc(sketch, "E252", {"start": v(15.5, 5) * mm, "mid": v(15.8, 4.3) * mm, "end": v(16.5, 4) * mm});
            skArc(sketch, "E253", {"start": v(18, -7.25) * mm, "mid": v(17.93, -7.07) * mm, "end": v(17.75, -7) * mm});
            skArc(sketch, "E254", {"start": v(17.75, 7) * mm, "mid": v(17.93, 7.07) * mm, "end": v(18, 7.25) * mm});
            skArc(sketch, "E255", {"start": v(18.3, 11.2) * mm, "mid": v(18.65, 11.35) * mm, "end": v(18.8, 11.7) * mm});
            skArc(sketch, "E256", {"start": v(18.8, -11.7) * mm, "mid": v(18.65, -11.35) * mm, "end": v(18.3, -11.2) * mm});
            skArc(sketch, "E257", {"start": v(20, -5.5) * mm, "mid": v(19.56, -4.44) * mm, "end": v(18.5, -4) * mm});
            skArc(sketch, "E258", {"start": v(18.5, 4) * mm, "mid": v(19.56, 4.44) * mm, "end": v(20, 5.5) * mm});
            skArc(sketch, "E259", {"start": v(10.75, 8.88) * mm, "mid": v(9.09, 7.2) * mm, "end": v(7.59, 5.38) * mm});
            skArc(sketch, "E260", {"start": v(7.59, -5.38) * mm, "mid": v(9.09, -7.2) * mm, "end": v(10.75, -8.88) * mm});
            skArc(sketch, "E261", {"start": v(13.51, 9.6) * mm, "mid": v(10.85, 7.26) * mm, "end": v(8.54, 4.58) * mm});
            skArc(sketch, "E262", {"start": v(8.54, -4.58) * mm, "mid": v(10.85, -7.26) * mm, "end": v(13.51, -9.6) * mm});
            skSolve(sketch);
        }
        {
            var Q0;
            Q0=qCreatedBy(makeId("Top.planeOp"),FACE);
            var sketch = newSketch(context, id + "F12", { "sketchPlane" : qUnion([Q0])});
            skLineSegment(sketch, "E263", {"start": v(0, 0) * mm, "end": v(-59.9, 0) * mm});
            skSolve(sketch);
        }
        {
            var Q0;
            Q0 = qSketchRegion(id + "F11", true);
            var Q1;
            Q1=sQuery(id+"F12.wireOp",EDGE,"E263");
            sweep(context, id + "F13", {"profiles" : qUnion([Q0]), "path" : qUnion([Q1])});
        }
    });
